# Revit family: E-310_RFA
name_source: partatom
category: Aparatos sanitarios
units: mm (PartAtom-declared; Revit-internal decimal feet)

## family parameters
Compartido = Sí
Corte con vacíos al cargar = No
Cota de conector redondo = Diámetro de uso
Número OmniClass = 23.45.55.17
Punto de cálculo de habitación = Sí
Se basa en plano de trabajo = No
Siempre vertical = Sí
Tipo de pieza = Normal
Título OmniClass = Mixing Faucets

## types (1)
- E-309
    Brass Chromed = Brass
    Comentarios de tipo = Lavatory Faucet Assemblies
    Data Sheet = https://www.helvex.com.mx
    Descripción = Monomando para fregadero E-310
    Elevación por defecto = 0"
    Fabricante = HELVEX S.A. de C.V.
    Imagen de tipo = E-310.jpg
    Inlet Threads = ½" - 14 NPSM
    Instructive = https://www.helvex.com.mx
    Max. Working Pressure = 85.3 psi
    Min. Working Pressure = 8.5 psi
    Modelo = E-310
    Support Base Diameter = 2"
    Total Height = 15"
    Total Length = 10"
    Total Width = 4"
    URL = https://www.helvex.com.mx
    Ébano = Ébano

## geometry (parser evidence)
native form markers: Sweep x3
no freeform markers — native parametric forms only
